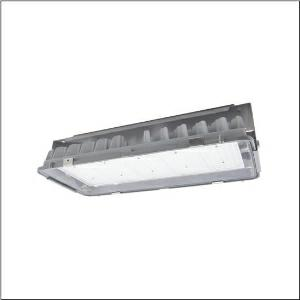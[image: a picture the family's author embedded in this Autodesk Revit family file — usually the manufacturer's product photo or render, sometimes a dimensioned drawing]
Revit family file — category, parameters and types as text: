
# Revit family: highbay_11xtreme_51hf82da4nma
name_source: partatom
category: Lighting Fixtures
units: mm (PartAtom-declared; Revit-internal decimal feet)

## family parameters
Cut with Voids When Loaded = No
Host = Face
Light Source = No
Part Type = Normal
Room Calculation Point = No
Round Connector Dimension = Use Diameter
Shared = No

## types (1)
- --- (1 x LED, 33700 lm, 187.7 W, 4000K)
    Apparent Load = 188 VA
    CIE Flux Codes = 84 96 100 100 100
    Color Rendering = 80
    Color Temperature = 4000K
    Default Elevation = 1800 mm
    Description = Highbay 11Xtreme, high bay luminaire, primary light control with lens, of PMMA, primary optical cover: cover, of toughened safety glass, light emission: direct distribution, primary light characteristic: symmetric, installation type: suspended mounting, surface-mounted, 1x LED module,for 1x LED, rated luminous flux: 33.700lm, luminous efficacy: 180lm/W, light colour: 840, colour temperature: 4000K, control gear: DALI 2, with cable H07RN-F 5x 1.5mm², mains connection: 220..240V, AC, 50/60Hz, cable length: 1,5m, rated input power: 188W, luminaire housing, of diecast aluminium, partly coated, silver, length: 595mm, width: 280mm, height: 195mm, protection rating (complete): IP66, insulation class (complete): insulation class I (protective earthing), certification: CE, ENEC, UKCA, protection symbol: D, ball protection: ball impact resistant according to DIN VDE 0710 part 13 (with chain suspension), impact resistance: IK08, permissible operating ambient temperature: -25..+45°C, reducing of maximum allowable ambient temperature of 5°C with ceiling mounting, packaging unit: 1 piece
    Height = 157 mm
    Lamp = 1 x LED
    Lamp Light Flux = 33700 lm
    Lamp Power = 187.7 W
    Lamp count = 1
    Length = 593 mm
    Luminous efficacy = 180 lm/W
    Manufacturer = Siteco
    ModVariant = No
    Model = 51HF82DA4NMA
    Mounting Place = Ceiling
    Mounting Type = Pendant
    Number of Poles = 1
    OnlyDefault = Yes
    Power Factor = 1
    Product Name = Highbay 11Xtreme
    Product group = high bay luminaire
    ProductGroupID = 902
    Protection Class = Protection class I
    Protection Degree = IP 66
    RLX_Detail_Level = 1
    RLX_Emergency_Light_Flux = 0 lm
    RLX_Emergency_Type = 0
    RLX_Emergency_Type_DB = No
    RlxData = <blob elided: 28377 chars, md5=d468c6e8>
    Socket = socket
    Standby Power = 0 W
    System Light Flux = 33700 lm
    System Power = 188 W
    Type Comments = factory setting: luminous flux: 100 % | dim-lin: 254 | 1255 mA
    Type Image = l_1258342.jpg
    URL = http://relux.com
    VarID = @adj_088197
    Voltage = 0 V
    Weight = 0.00 kg
    Width = 568 mm

## geometry (parser evidence)
native form markers: Blend x4, Sweep x9
no freeform markers — native parametric forms only
